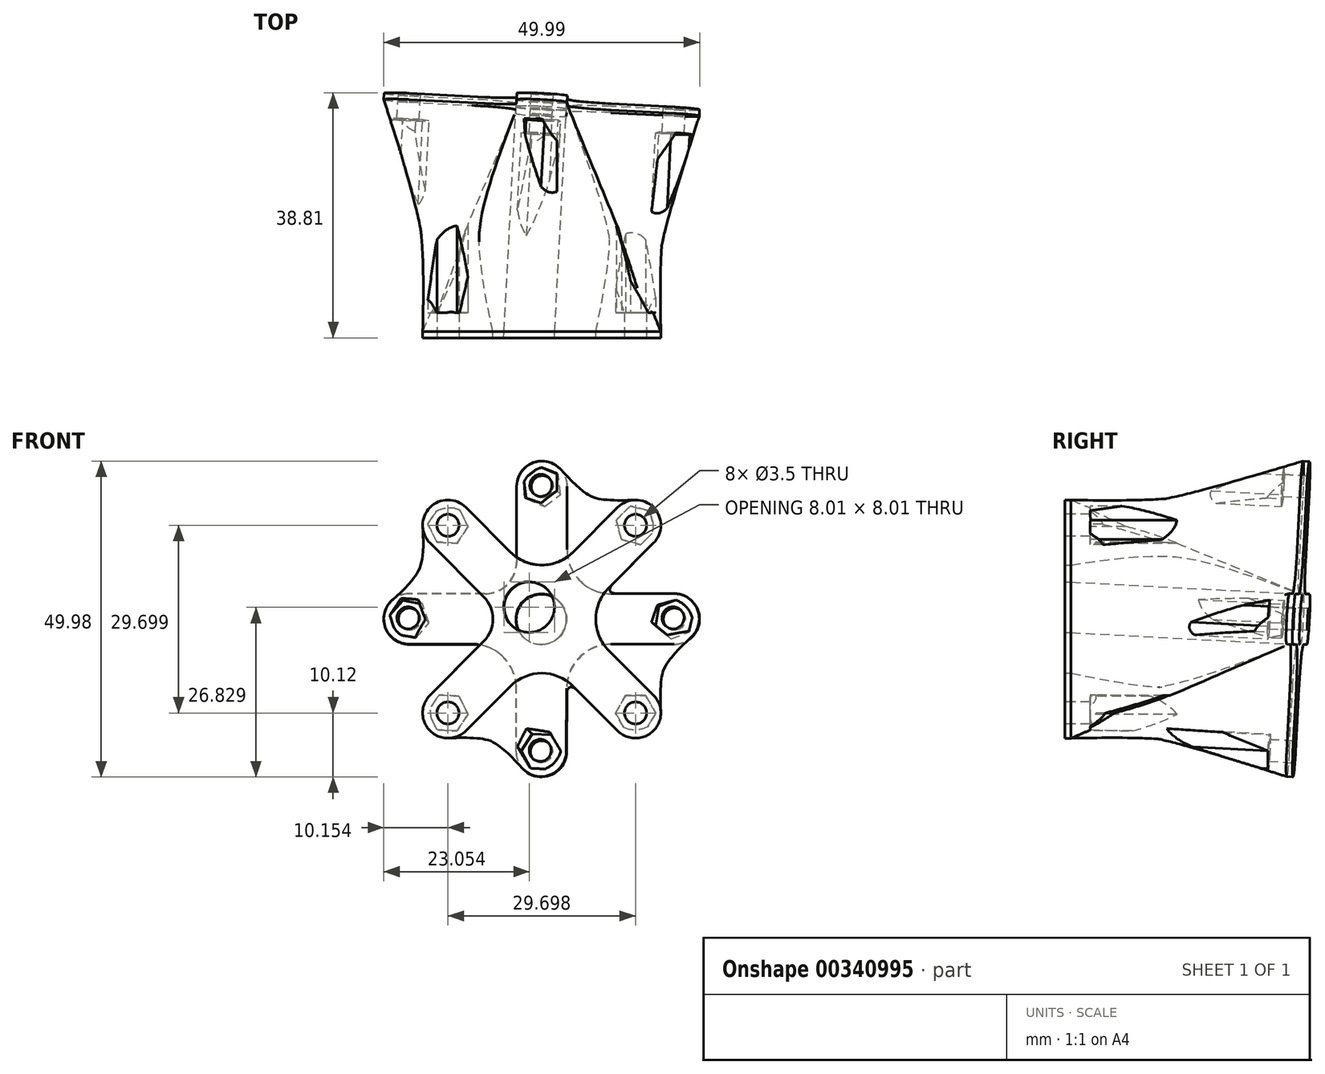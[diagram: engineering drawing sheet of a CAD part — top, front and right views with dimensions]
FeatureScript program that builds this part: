
annotation { "Feature Type Name" : "Feature", "Feature Type Description" : "" }
export const myFeature = defineFeature(function(context is Context, id is Id, definition is map)
    precondition{}
    {
        {
            var Q0;
            Q0=qCreatedBy(makeId("Front.planeOp"),FACE);
            var sketch = newSketch(context, id + "F0", { "sketchPlane" : qUnion([Q0])});
            skLineSegment(sketch, "E0", {"start": v(-2.67, 4.2) * mm, "end": v(-2.67, 70.2) * mm});
            skFitSpline(sketch, "E1", {"points": [v(-2.67, 70.2) * mm, v(4.36, 79.68) * mm, v(10.86, 84.56) * mm, v(19.6, 87.5) * mm, v(32.83, 88.7) * mm], "startDerivative": vector(17.44, 44.03) * mm, "endDerivative": vector(48.5, 0) * mm});
            skFitSpline(sketch, "E2", {"points": [v(-2.67, 4.2) * mm, v(0, -1.2) * mm, v(6.58, -5.59) * mm, v(16.1, -7.75) * mm, v(24.4, -8.77) * mm, v(32.83, -9.43) * mm], "startDerivative": vector(11.57, -32.78) * mm, "endDerivative": vector(34.9, 0) * mm});
            skFitSpline(sketch, "E3.MirrorCS", {"points": [v(68.33, 70.2) * mm, v(61.3, 79.68) * mm, v(54.8, 84.56) * mm, v(46.08, 87.5) * mm, v(32.83, 88.7) * mm], "startDerivative": vector(-17.44, 44.03) * mm, "endDerivative": vector(-48.5, 0) * mm});
            skLineSegment(sketch, "E4.MirrorCS", {"start": v(68.33, 4.2) * mm, "end": v(68.33, 70.2) * mm});
            skFitSpline(sketch, "E5.MirrorCS", {"points": [v(68.33, 4.2) * mm, v(65.67, -1.2) * mm, v(59.09, -5.59) * mm, v(49.56, -7.75) * mm, v(41.27, -8.77) * mm, v(32.83, -9.43) * mm], "startDerivative": vector(-11.57, -32.78) * mm, "endDerivative": vector(-34.9, 0) * mm});
            skCircle(sketch, "E6", {"center": v(16.13, 65.4) * mm, "radius": 1.75 * mm});
            skCircle(sketch, "E7", {"center": v(16.13, 36) * mm, "radius": 1.75 * mm});
            skCircle(sketch, "E8.MirrorC", {"center": v(45.53, 65.4) * mm, "radius": 1.75 * mm});
            skCircle(sketch, "E9.MirrorC", {"center": v(45.53, 36) * mm, "radius": 1.75 * mm});
            skCircle(sketch, "E10", {"center": v(30.83, 50.7) * mm, "radius": 10 * mm});
            skSolve(sketch);
        }
        {
            var Q0;
            Q0=qCreatedBy(makeId("Front.planeOp"),FACE);
            cPlane(context, id + "F1", {"entities" : qUnion([Q0]), "cplaneType" : CPlaneType.OFFSET, "offset" : 38 * mm, "oppositeDirection" : true, "width" : 150 * mm, "height" : 150 * mm});
        }
        {
            var Q0;
            Q0=qCreatedBy(id+"F1.planeOp",FACE);
            var sketch = newSketch(context, id + "F2", { "sketchPlane" : qUnion([Q0])});
            skLineSegment(sketch, "E11", {"start": v(30.83, 3.24) * mm, "end": v(30.83, 83.87) * mm, "construction": true});
            skLineSegment(sketch, "E12", {"start": v(-5.05, 50.7) * mm, "end": v(67.53, 50.7) * mm, "construction": true});
            skLineSegment(sketch, "E13", {"start": v(26.83, 71.7) * mm, "end": v(26.83, 59.7) * mm});
            skLineSegment(sketch, "E14.MirrorCS", {"start": v(34.83, 71.7) * mm, "end": v(34.83, 61.7) * mm});
            skArc(sketch, "E15", {"start": v(34.83, 71.7) * mm, "mid": v(30.83, 75.7) * mm, "end": v(26.83, 71.7) * mm});
            skArc(sketch, "E16.MirrorCS", {"start": v(34.83, 29.7) * mm, "mid": v(30.83, 25.7) * mm, "end": v(26.83, 29.7) * mm});
            skLineSegment(sketch, "E17", {"start": v(21.83, 54.7) * mm, "end": v(9.83, 54.7) * mm});
            skLineSegment(sketch, "E18.MirrorCS", {"start": v(51.83, 46.7) * mm, "end": v(41.83, 46.7) * mm});
            skArc(sketch, "E19", {"start": v(51.83, 54.7) * mm, "mid": v(55.83, 50.7) * mm, "end": v(51.83, 46.7) * mm});
            skArc(sketch, "E20.MirrorCS", {"start": v(9.83, 54.7) * mm, "mid": v(5.83, 50.7) * mm, "end": v(9.83, 46.7) * mm});
            skLineSegment(sketch, "E21", {"start": v(40.15, 65.4) * mm, "end": v(21.95, 65.4) * mm, "construction": true});
            skCircle(sketch, "E22", {"center": v(30.83, 71.7) * mm, "radius": 1.75 * mm});
            skCircle(sketch, "E23", {"center": v(30.83, 29.7) * mm, "radius": 1.75 * mm});
            skCircle(sketch, "E24", {"center": v(51.83, 50.7) * mm, "radius": 1.75 * mm});
            skCircle(sketch, "E25", {"center": v(9.83, 50.7) * mm, "radius": 1.75 * mm});
            skPoint(sketch, "E26.newPointA", {"position": v(26.83, 29.7) * mm});
            skPoint(sketch, "E26.newPointB", {"position": v(51.83, 54.7) * mm});
            skArc(sketch, "E26.filletArc", {"start": v(21.83, 54.7) * mm, "mid": v(25.37, 56.17) * mm, "end": v(26.83, 59.7) * mm});
            skLineSegment(sketch, "E27", {"start": v(51.83, 54.7) * mm, "end": v(41.83, 54.7) * mm});
            skLineSegment(sketch, "E28", {"start": v(26.83, 29.7) * mm, "end": v(26.83, 39.7) * mm});
            skPoint(sketch, "E29.newPointA", {"position": v(34.83, 29.7) * mm});
            skArc(sketch, "E29.filletArc", {"start": v(34.83, 61.7) * mm, "mid": v(36.88, 56.76) * mm, "end": v(41.83, 54.7) * mm});
            skLineSegment(sketch, "E30", {"start": v(34.83, 29.7) * mm, "end": v(34.83, 39.7) * mm});
            skPoint(sketch, "E31.newPointB", {"position": v(9.83, 46.7) * mm});
            skArc(sketch, "E31.filletArc", {"start": v(41.83, 46.7) * mm, "mid": v(36.88, 44.66) * mm, "end": v(34.83, 39.7) * mm});
            skLineSegment(sketch, "E32", {"start": v(9.83, 46.7) * mm, "end": v(19.83, 46.7) * mm});
            skArc(sketch, "E33.filletArc", {"start": v(26.83, 39.7) * mm, "mid": v(24.78, 44.66) * mm, "end": v(19.83, 46.7) * mm});
            skCircle(sketch, "E34", {"center": v(30.83, 50.7) * mm, "radius": 4 * mm});
            skSolve(sketch);
        }
        {
            var Q0;
            Q0=makeQuery(id+"F2.imprint","IMPRINT",FACE,{"disambiguationData":[TD([[makeQuery(id+"F2.imprint","IMPRINT",EDGE,{"derivedFrom":sQuery(id+"F2.wireOp",EDGE,"E23")}),1.0]])]});
            var Q1;
            Q1=makeQuery(id+"F2.imprint","IMPRINT",FACE,{"disambiguationData":[TD([[makeQuery(id+"F2.imprint","IMPRINT",EDGE,{"derivedFrom":sQuery(id+"F2.wireOp",EDGE,"E34")}),1.0]])]});
            var Q2;
            Q2=makeQuery(id+"F2.imprint","IMPRINT",FACE,{"disambiguationData":[TD([[makeQuery(id+"F2.imprint","IMPRINT",EDGE,{"derivedFrom":sQuery(id+"F2.wireOp",EDGE,"E25")}),1.0]])]});
            var Q3;
            Q3=makeQuery(id+"F2.imprint","IMPRINT",FACE,{"disambiguationData":[TD([[makeQuery(id+"F2.imprint","IMPRINT",EDGE,{"derivedFrom":sQuery(id+"F2.wireOp",EDGE,"E22")}),1.0]])]});
            var Q4;
            Q4=makeQuery(id+"F2.imprint","IMPRINT",FACE,{"disambiguationData":[TD([[makeQuery(id+"F2.imprint","IMPRINT",EDGE,{"derivedFrom":sQuery(id+"F2.wireOp",EDGE,"E24")}),1.0]])]});
            var Q5;
            Q5=makeQuery(id+"F2.imprint","IMPRINT",FACE,{"disambiguationData":[TD([[makeQuery(id+"F2.imprint","IMPRINT",EDGE,{"derivedFrom":sQuery(id+"F2.wireOp",EDGE,"E13")}),1.0]])]});
            extrude(context, id + "F3", {"entities" : qUnion([Q0, Q1, Q2, Q3, Q4, Q5]), "depth" : 1 * mm, "offsetDistance" : 25 * mm});
        }
        {
            var Q0;
            Q0=makeQuery(id+"F3.opExtrude","SWEPT_BODY",BODY,{"disambiguationData":[OSD([sQuery(id+"F2.wireOp",EDGE,"E13"),sQuery(id+"F2.wireOp",EDGE,"E14.MirrorCS"),sQuery(id+"F2.wireOp",EDGE,"E15"),sQuery(id+"F2.wireOp",EDGE,"E16.MirrorCS"),sQuery(id+"F2.wireOp",EDGE,"E17"),sQuery(id+"F2.wireOp",EDGE,"E18.MirrorCS"),sQuery(id+"F2.wireOp",EDGE,"E19"),sQuery(id+"F2.wireOp",EDGE,"E20.MirrorCS"),sQuery(id+"F2.wireOp",EDGE,"E26.filletArc"),sQuery(id+"F2.wireOp",EDGE,"E27"),sQuery(id+"F2.wireOp",EDGE,"E28"),sQuery(id+"F2.wireOp",EDGE,"E29.filletArc"),sQuery(id+"F2.wireOp",EDGE,"E30"),sQuery(id+"F2.wireOp",EDGE,"E31.filletArc"),sQuery(id+"F2.wireOp",EDGE,"E32"),sQuery(id+"F2.wireOp",EDGE,"E33.filletArc")])]});
            transform(context, id + "F4", {"entities" : qUnion([Q0]), "transformType" : TransformType.TRANSLATION_3D, "dx" : 0 * mm, "dy" : -36 * mm, "dz" : 0 * mm, "makeCopy" : true});
        }
        {
            var Q0;
            Q0=makeQuery(id+"F3.opExtrude","SWEPT_BODY",BODY,{"disambiguationData":[OSD([sQuery(id+"F2.wireOp",EDGE,"E13"),sQuery(id+"F2.wireOp",EDGE,"E14.MirrorCS"),sQuery(id+"F2.wireOp",EDGE,"E15"),sQuery(id+"F2.wireOp",EDGE,"E16.MirrorCS"),sQuery(id+"F2.wireOp",EDGE,"E17"),sQuery(id+"F2.wireOp",EDGE,"E18.MirrorCS"),sQuery(id+"F2.wireOp",EDGE,"E19"),sQuery(id+"F2.wireOp",EDGE,"E20.MirrorCS"),sQuery(id+"F2.wireOp",EDGE,"E26.filletArc"),sQuery(id+"F2.wireOp",EDGE,"E27"),sQuery(id+"F2.wireOp",EDGE,"E28"),sQuery(id+"F2.wireOp",EDGE,"E29.filletArc"),sQuery(id+"F2.wireOp",EDGE,"E30"),sQuery(id+"F2.wireOp",EDGE,"E31.filletArc"),sQuery(id+"F2.wireOp",EDGE,"E32"),sQuery(id+"F2.wireOp",EDGE,"E33.filletArc")])]});
            var Q1;
            Q1=makeQuery(id+"F3.opExtrude","CAP_EDGE",EDGE,{"disambiguationData":[OSD([sQuery(id+"F2.wireOp",EDGE,"E30")])],"isStart":true});
            transform(context, id + "F5", {"entities" : qUnion([Q0]), "transformType" : TransformType.ROTATION, "transformAxis" : qUnion([Q1]), "angle" : 3 * degree, "oppositeDirection" : true, "makeCopy" : false});
        }
        {
            var Q0;
            Q0=makeQuery(id+"F3.opExtrude","SWEPT_BODY",BODY,{"disambiguationData":[OSD([sQuery(id+"F2.wireOp",EDGE,"E13"),sQuery(id+"F2.wireOp",EDGE,"E14.MirrorCS"),sQuery(id+"F2.wireOp",EDGE,"E15"),sQuery(id+"F2.wireOp",EDGE,"E16.MirrorCS"),sQuery(id+"F2.wireOp",EDGE,"E17"),sQuery(id+"F2.wireOp",EDGE,"E18.MirrorCS"),sQuery(id+"F2.wireOp",EDGE,"E19"),sQuery(id+"F2.wireOp",EDGE,"E20.MirrorCS"),sQuery(id+"F2.wireOp",EDGE,"E26.filletArc"),sQuery(id+"F2.wireOp",EDGE,"E27"),sQuery(id+"F2.wireOp",EDGE,"E28"),sQuery(id+"F2.wireOp",EDGE,"E29.filletArc"),sQuery(id+"F2.wireOp",EDGE,"E30"),sQuery(id+"F2.wireOp",EDGE,"E31.filletArc"),sQuery(id+"F2.wireOp",EDGE,"E32"),sQuery(id+"F2.wireOp",EDGE,"E33.filletArc")])]});
            var Q1;
            Q1=makeQuery(id+"F3.opExtrude","CAP_EDGE",EDGE,{"disambiguationData":[OSD([sQuery(id+"F2.wireOp",EDGE,"E32")])],"isStart":true});
            transform(context, id + "F6", {"entities" : qUnion([Q0]), "transformType" : TransformType.ROTATION, "transformAxis" : qUnion([Q1]), "angle" : 3 * degree, "oppositeDirection" : true, "makeCopy" : false});
        }
        {
            var Q0;
            Q0=makeQuery(id+"F4.opPattern","COPY",BODY,{"derivedFrom":makeQuery(id+"FqoNIN35yEYZdyi_0.opExtrude","SWEPT_BODY",BODY,{"disambiguationData":[OSD([sQuery(id+"F2.wireOp",EDGE,"E13"),sQuery(id+"F2.wireOp",EDGE,"E14.MirrorCS"),sQuery(id+"F2.wireOp",EDGE,"E15"),sQuery(id+"F2.wireOp",EDGE,"E16.MirrorCS"),sQuery(id+"F2.wireOp",EDGE,"E17"),sQuery(id+"F2.wireOp",EDGE,"E18.MirrorCS"),sQuery(id+"F2.wireOp",EDGE,"E19"),sQuery(id+"F2.wireOp",EDGE,"E20.MirrorCS"),sQuery(id+"F2.wireOp",EDGE,"E22"),sQuery(id+"F2.wireOp",EDGE,"E23"),sQuery(id+"F2.wireOp",EDGE,"E24"),sQuery(id+"F2.wireOp",EDGE,"E25"),sQuery(id+"F2.wireOp",EDGE,"E26.filletArc"),sQuery(id+"F2.wireOp",EDGE,"E27"),sQuery(id+"F2.wireOp",EDGE,"E28"),sQuery(id+"F2.wireOp",EDGE,"E29.filletArc"),sQuery(id+"F2.wireOp",EDGE,"E30"),sQuery(id+"F2.wireOp",EDGE,"E31.filletArc"),sQuery(id+"F2.wireOp",EDGE,"E32"),sQuery(id+"F2.wireOp",EDGE,"E33.filletArc"),sQuery(id+"F2.wireOp",EDGE,"E34")])]}),"instanceName":"1"});
            var Q1;
            Q1=makeQuery(id+"F4.opPattern","COPY",BODY,{"derivedFrom":makeQuery(id+"F3.opExtrude","SWEPT_BODY",BODY,{"disambiguationData":[OSD([sQuery(id+"F2.wireOp",EDGE,"E13"),sQuery(id+"F2.wireOp",EDGE,"E14.MirrorCS"),sQuery(id+"F2.wireOp",EDGE,"E15"),sQuery(id+"F2.wireOp",EDGE,"E16.MirrorCS"),sQuery(id+"F2.wireOp",EDGE,"E17"),sQuery(id+"F2.wireOp",EDGE,"E18.MirrorCS"),sQuery(id+"F2.wireOp",EDGE,"E19"),sQuery(id+"F2.wireOp",EDGE,"E20.MirrorCS"),sQuery(id+"F2.wireOp",EDGE,"E26.filletArc"),sQuery(id+"F2.wireOp",EDGE,"E27"),sQuery(id+"F2.wireOp",EDGE,"E28"),sQuery(id+"F2.wireOp",EDGE,"E29.filletArc"),sQuery(id+"F2.wireOp",EDGE,"E30"),sQuery(id+"F2.wireOp",EDGE,"E31.filletArc"),sQuery(id+"F2.wireOp",EDGE,"E32"),sQuery(id+"F2.wireOp",EDGE,"E33.filletArc")])]}),"instanceName":"1"});
            var Q2;
            Q2=sQuery(id+"F0.wireOp",EDGE,"E10");
            transform(context, id + "F7", {"entities" : qUnion([Q0, Q1]), "transformType" : TransformType.ROTATION, "transformAxis" : qUnion([Q2]), "angle" : 45 * degree, "makeCopy" : false});
        }
        {
            var Q0;
            Q0=makeQuery(id+"F3.opExtrude","CAP_FACE",FACE,{"disambiguationData":[OSD([sQuery(id+"F2.wireOp",EDGE,"E13"),sQuery(id+"F2.wireOp",EDGE,"E14.MirrorCS"),sQuery(id+"F2.wireOp",EDGE,"E15"),sQuery(id+"F2.wireOp",EDGE,"E16.MirrorCS"),sQuery(id+"F2.wireOp",EDGE,"E17"),sQuery(id+"F2.wireOp",EDGE,"E18.MirrorCS"),sQuery(id+"F2.wireOp",EDGE,"E19"),sQuery(id+"F2.wireOp",EDGE,"E20.MirrorCS"),sQuery(id+"F2.wireOp",EDGE,"E26.filletArc"),sQuery(id+"F2.wireOp",EDGE,"E27"),sQuery(id+"F2.wireOp",EDGE,"E28"),sQuery(id+"F2.wireOp",EDGE,"E29.filletArc"),sQuery(id+"F2.wireOp",EDGE,"E30"),sQuery(id+"F2.wireOp",EDGE,"E31.filletArc"),sQuery(id+"F2.wireOp",EDGE,"E32"),sQuery(id+"F2.wireOp",EDGE,"E33.filletArc")])],"isStart":false});
            var Q1;
            Q1=makeQuery(id+"F4.opPattern","COPY",FACE,{"derivedFrom":makeQuery(id+"F3.opExtrude","CAP_FACE",FACE,{"disambiguationData":[OSD([sQuery(id+"F2.wireOp",EDGE,"E13"),sQuery(id+"F2.wireOp",EDGE,"E14.MirrorCS"),sQuery(id+"F2.wireOp",EDGE,"E15"),sQuery(id+"F2.wireOp",EDGE,"E16.MirrorCS"),sQuery(id+"F2.wireOp",EDGE,"E17"),sQuery(id+"F2.wireOp",EDGE,"E18.MirrorCS"),sQuery(id+"F2.wireOp",EDGE,"E19"),sQuery(id+"F2.wireOp",EDGE,"E20.MirrorCS"),sQuery(id+"F2.wireOp",EDGE,"E26.filletArc"),sQuery(id+"F2.wireOp",EDGE,"E27"),sQuery(id+"F2.wireOp",EDGE,"E28"),sQuery(id+"F2.wireOp",EDGE,"E29.filletArc"),sQuery(id+"F2.wireOp",EDGE,"E30"),sQuery(id+"F2.wireOp",EDGE,"E31.filletArc"),sQuery(id+"F2.wireOp",EDGE,"E32"),sQuery(id+"F2.wireOp",EDGE,"E33.filletArc")])],"isStart":true}),"instanceName":"1"});
            loft(context, id + "F8", {"sheetProfilesArray" : [{ "sheetProfileEntities" : qUnion([Q0]) }, { "sheetProfileEntities" : qUnion([Q1]) }]});
        }
        {
            var Q0;
            Q0=makeQuery(id+"F4.opPattern","COPY",FACE,{"derivedFrom":makeQuery(id+"F3.opExtrude","CAP_FACE",FACE,{"disambiguationData":[OSD([sQuery(id+"F2.wireOp",EDGE,"E13"),sQuery(id+"F2.wireOp",EDGE,"E14.MirrorCS"),sQuery(id+"F2.wireOp",EDGE,"E15"),sQuery(id+"F2.wireOp",EDGE,"E16.MirrorCS"),sQuery(id+"F2.wireOp",EDGE,"E17"),sQuery(id+"F2.wireOp",EDGE,"E18.MirrorCS"),sQuery(id+"F2.wireOp",EDGE,"E19"),sQuery(id+"F2.wireOp",EDGE,"E20.MirrorCS"),sQuery(id+"F2.wireOp",EDGE,"E26.filletArc"),sQuery(id+"F2.wireOp",EDGE,"E27"),sQuery(id+"F2.wireOp",EDGE,"E28"),sQuery(id+"F2.wireOp",EDGE,"E29.filletArc"),sQuery(id+"F2.wireOp",EDGE,"E30"),sQuery(id+"F2.wireOp",EDGE,"E31.filletArc"),sQuery(id+"F2.wireOp",EDGE,"E32"),sQuery(id+"F2.wireOp",EDGE,"E33.filletArc")])],"isStart":false}),"instanceName":"1"});
            var sketch = newSketch(context, id + "F9", { "sketchPlane" : qUnion([Q0])});
            skLineSegment(sketch, "E35", {"start": v(48.51, 68.39) * mm, "end": v(13.16, 33.03) * mm, "construction": true});
            skLineSegment(sketch, "E36", {"start": v(13.16, 68.39) * mm, "end": v(48.51, 33.03) * mm, "construction": true});
            skCircle(sketch, "E37", {"center": v(45.68, 35.86) * mm, "radius": 1.75 * mm});
            skCircle(sketch, "E38", {"center": v(45.68, 65.56) * mm, "radius": 1.75 * mm});
            skCircle(sketch, "E39", {"center": v(15.98, 35.86) * mm, "radius": 1.75 * mm});
            skCircle(sketch, "E40", {"center": v(15.98, 65.56) * mm, "radius": 1.75 * mm});
            skSolve(sketch);
        }
        {
            var Q0;
            Q0=makeQuery(id+"F9.imprint","IMPRINT",FACE,{"disambiguationData":[TD([[makeQuery(id+"F9.imprint","IMPRINT",EDGE,{"derivedFrom":sQuery(id+"F9.wireOp",EDGE,"E40")}),1.0]])]});
            var Q1;
            Q1=makeQuery(id+"F9.imprint","IMPRINT",FACE,{"disambiguationData":[TD([[makeQuery(id+"F9.imprint","IMPRINT",EDGE,{"derivedFrom":sQuery(id+"F9.wireOp",EDGE,"E38")}),1.0]])]});
            var Q2;
            Q2=makeQuery(id+"F9.imprint","IMPRINT",FACE,{"disambiguationData":[TD([[makeQuery(id+"F9.imprint","IMPRINT",EDGE,{"derivedFrom":sQuery(id+"F9.wireOp",EDGE,"E39")}),1.0]])]});
            var Q3;
            Q3=makeQuery(id+"F9.imprint","IMPRINT",FACE,{"disambiguationData":[TD([[makeQuery(id+"F9.imprint","IMPRINT",EDGE,{"derivedFrom":sQuery(id+"F9.wireOp",EDGE,"E37")}),1.0]])]});
            extrude(context, id + "F10", {"entities" : qUnion([Q0, Q1, Q2, Q3]), "oppositeDirection" : true, "depth" : 25 * mm, "offsetDistance" : 25 * mm});
        }
        {
            var Q0;
            Q0=makeQuery(id+"F10.opExtrude","SWEPT_BODY",BODY,{"disambiguationData":[OSD([sQuery(id+"F9.wireOp",EDGE,"E40")])]});
            var Q1;
            Q1=makeQuery(id+"F10.opExtrude","SWEPT_BODY",BODY,{"disambiguationData":[OSD([sQuery(id+"F9.wireOp",EDGE,"E39")])]});
            var Q2;
            Q2=makeQuery(id+"F10.opExtrude","SWEPT_BODY",BODY,{"disambiguationData":[OSD([sQuery(id+"F9.wireOp",EDGE,"E38")])]});
            var Q3;
            Q3=makeQuery(id+"F10.opExtrude","SWEPT_BODY",BODY,{"disambiguationData":[OSD([sQuery(id+"F9.wireOp",EDGE,"E37")])]});
            var Q4;
            Q4=makeQuery(id+"F8.opLoft","SWEPT_BODY",BODY,{"disambiguationData":[OSD([sQuery(id+"F2.wireOp",EDGE,"E13"),sQuery(id+"F2.wireOp",EDGE,"E14.MirrorCS"),sQuery(id+"F2.wireOp",EDGE,"E15"),sQuery(id+"F2.wireOp",EDGE,"E16.MirrorCS"),sQuery(id+"F2.wireOp",EDGE,"E17"),sQuery(id+"F2.wireOp",EDGE,"E18.MirrorCS"),sQuery(id+"F2.wireOp",EDGE,"E19"),sQuery(id+"F2.wireOp",EDGE,"E20.MirrorCS"),sQuery(id+"F2.wireOp",EDGE,"E26.filletArc"),sQuery(id+"F2.wireOp",EDGE,"E27"),sQuery(id+"F2.wireOp",EDGE,"E28"),sQuery(id+"F2.wireOp",EDGE,"E29.filletArc"),sQuery(id+"F2.wireOp",EDGE,"E30"),sQuery(id+"F2.wireOp",EDGE,"E31.filletArc"),sQuery(id+"F2.wireOp",EDGE,"E32"),sQuery(id+"F2.wireOp",EDGE,"E33.filletArc")])]});
            var Q5;
            Q5=makeQuery(id+"F4.opPattern","COPY",BODY,{"derivedFrom":makeQuery(id+"F3.opExtrude","SWEPT_BODY",BODY,{"disambiguationData":[OSD([sQuery(id+"F2.wireOp",EDGE,"E13"),sQuery(id+"F2.wireOp",EDGE,"E14.MirrorCS"),sQuery(id+"F2.wireOp",EDGE,"E15"),sQuery(id+"F2.wireOp",EDGE,"E16.MirrorCS"),sQuery(id+"F2.wireOp",EDGE,"E17"),sQuery(id+"F2.wireOp",EDGE,"E18.MirrorCS"),sQuery(id+"F2.wireOp",EDGE,"E19"),sQuery(id+"F2.wireOp",EDGE,"E20.MirrorCS"),sQuery(id+"F2.wireOp",EDGE,"E26.filletArc"),sQuery(id+"F2.wireOp",EDGE,"E27"),sQuery(id+"F2.wireOp",EDGE,"E28"),sQuery(id+"F2.wireOp",EDGE,"E29.filletArc"),sQuery(id+"F2.wireOp",EDGE,"E30"),sQuery(id+"F2.wireOp",EDGE,"E31.filletArc"),sQuery(id+"F2.wireOp",EDGE,"E32"),sQuery(id+"F2.wireOp",EDGE,"E33.filletArc")])]}),"instanceName":"1"});
            var Q6;
            Q6=makeQuery(id+"F3.opExtrude","SWEPT_BODY",BODY,{"disambiguationData":[OSD([sQuery(id+"F2.wireOp",EDGE,"E13"),sQuery(id+"F2.wireOp",EDGE,"E14.MirrorCS"),sQuery(id+"F2.wireOp",EDGE,"E15"),sQuery(id+"F2.wireOp",EDGE,"E16.MirrorCS"),sQuery(id+"F2.wireOp",EDGE,"E17"),sQuery(id+"F2.wireOp",EDGE,"E18.MirrorCS"),sQuery(id+"F2.wireOp",EDGE,"E19"),sQuery(id+"F2.wireOp",EDGE,"E20.MirrorCS"),sQuery(id+"F2.wireOp",EDGE,"E26.filletArc"),sQuery(id+"F2.wireOp",EDGE,"E27"),sQuery(id+"F2.wireOp",EDGE,"E28"),sQuery(id+"F2.wireOp",EDGE,"E29.filletArc"),sQuery(id+"F2.wireOp",EDGE,"E30"),sQuery(id+"F2.wireOp",EDGE,"E31.filletArc"),sQuery(id+"F2.wireOp",EDGE,"E32"),sQuery(id+"F2.wireOp",EDGE,"E33.filletArc")])]});
            booleanBodies(context, id + "F11", {"operationType" : BooleanOperationType.SUBTRACTION, "tools" : qUnion([Q0, Q1, Q2, Q3]), "targets" : qUnion([Q4, Q5, Q6])});
        }
        {
            var Q0;
            Q0=makeQuery(id+"F3.opExtrude","CAP_FACE",FACE,{"disambiguationData":[OSD([sQuery(id+"F2.wireOp",EDGE,"E13"),sQuery(id+"F2.wireOp",EDGE,"E14.MirrorCS"),sQuery(id+"F2.wireOp",EDGE,"E15"),sQuery(id+"F2.wireOp",EDGE,"E16.MirrorCS"),sQuery(id+"F2.wireOp",EDGE,"E17"),sQuery(id+"F2.wireOp",EDGE,"E18.MirrorCS"),sQuery(id+"F2.wireOp",EDGE,"E19"),sQuery(id+"F2.wireOp",EDGE,"E20.MirrorCS"),sQuery(id+"F2.wireOp",EDGE,"E26.filletArc"),sQuery(id+"F2.wireOp",EDGE,"E27"),sQuery(id+"F2.wireOp",EDGE,"E28"),sQuery(id+"F2.wireOp",EDGE,"E29.filletArc"),sQuery(id+"F2.wireOp",EDGE,"E30"),sQuery(id+"F2.wireOp",EDGE,"E31.filletArc"),sQuery(id+"F2.wireOp",EDGE,"E32"),sQuery(id+"F2.wireOp",EDGE,"E33.filletArc")])],"isStart":true});
            var sketch = newSketch(context, id + "F12", { "sketchPlane" : qUnion([Q0])});
            skCircle(sketch, "E41.cCircle", {"center": v(-29, 73.65) * mm, "radius": 2.75 * mm, "construction": true});
            skLineSegment(sketch, "E41.0", {"start": v(-26.45, 71.75) * mm, "end": v(-29.37, 70.5) * mm});
            skLineSegment(sketch, "E41.1", {"start": v(-29.37, 70.5) * mm, "end": v(-31.92, 72.4) * mm});
            skLineSegment(sketch, "E41.2", {"start": v(-31.92, 72.4) * mm, "end": v(-31.55, 75.54) * mm});
            skLineSegment(sketch, "E41.3", {"start": v(-31.55, 75.54) * mm, "end": v(-28.63, 76.8) * mm});
            skLineSegment(sketch, "E41.4", {"start": v(-28.63, 76.8) * mm, "end": v(-26.08, 74.9) * mm});
            skLineSegment(sketch, "E41.5", {"start": v(-26.08, 74.9) * mm, "end": v(-26.45, 71.75) * mm});
            skPoint(sketch, "E41.0.midPoint", {"position": v(-27.91, 71.12) * mm});
            skCircle(sketch, "E42.cCircle", {"center": v(-7.94, 52.7) * mm, "radius": 2.75 * mm, "construction": true});
            skLineSegment(sketch, "E42.0", {"start": v(-5.84, 50.32) * mm, "end": v(-8.96, 49.7) * mm});
            skLineSegment(sketch, "E42.1", {"start": v(-8.96, 49.7) * mm, "end": v(-11.05, 52.08) * mm});
            skLineSegment(sketch, "E42.2", {"start": v(-11.05, 52.08) * mm, "end": v(-10.04, 55.09) * mm});
            skLineSegment(sketch, "E42.3", {"start": v(-10.04, 55.09) * mm, "end": v(-6.93, 55.71) * mm});
            skLineSegment(sketch, "E42.4", {"start": v(-6.93, 55.71) * mm, "end": v(-4.83, 53.33) * mm});
            skLineSegment(sketch, "E42.5", {"start": v(-4.83, 53.33) * mm, "end": v(-5.84, 50.32) * mm});
            skPoint(sketch, "E42.0.midPoint", {"position": v(-7.4, 50) * mm});
            skCircle(sketch, "E43.cCircle", {"center": v(-28.88, 31.65) * mm, "radius": 2.75 * mm, "construction": true});
            skLineSegment(sketch, "E43.0", {"start": v(-25.71, 31.76) * mm, "end": v(-27.2, 28.96) * mm});
            skLineSegment(sketch, "E43.1", {"start": v(-27.2, 28.96) * mm, "end": v(-30.37, 28.84) * mm});
            skLineSegment(sketch, "E43.2", {"start": v(-30.37, 28.84) * mm, "end": v(-32.06, 31.54) * mm});
            skLineSegment(sketch, "E43.3", {"start": v(-32.06, 31.54) * mm, "end": v(-30.57, 34.34) * mm});
            skLineSegment(sketch, "E43.4", {"start": v(-30.57, 34.34) * mm, "end": v(-27.4, 34.45) * mm});
            skLineSegment(sketch, "E43.5", {"start": v(-27.4, 34.45) * mm, "end": v(-25.71, 31.76) * mm});
            skPoint(sketch, "E43.0.midPoint", {"position": v(-26.45, 30.36) * mm});
            skCircle(sketch, "E44.cCircle", {"center": v(-49.94, 52.6) * mm, "radius": 2.75 * mm, "construction": true});
            skLineSegment(sketch, "E44.0", {"start": v(-46.97, 51.48) * mm, "end": v(-49.41, 49.46) * mm});
            skLineSegment(sketch, "E44.1", {"start": v(-49.41, 49.46) * mm, "end": v(-52.4, 50.57) * mm});
            skLineSegment(sketch, "E44.2", {"start": v(-52.4, 50.57) * mm, "end": v(-52.92, 53.7) * mm});
            skLineSegment(sketch, "E44.3", {"start": v(-52.92, 53.7) * mm, "end": v(-50.47, 55.72) * mm});
            skLineSegment(sketch, "E44.4", {"start": v(-50.47, 55.72) * mm, "end": v(-47.5, 54.61) * mm});
            skLineSegment(sketch, "E44.5", {"start": v(-47.5, 54.61) * mm, "end": v(-46.97, 51.48) * mm});
            skPoint(sketch, "E44.0.midPoint", {"position": v(-48.2, 50.47) * mm});
            skSolve(sketch);
        }
        {
            var Q0;
            Q0=makeQuery(id+"F12.imprint","IMPRINT",FACE,{"disambiguationData":[TD([[makeQuery(id+"F12.imprint","IMPRINT",EDGE,{"derivedFrom":sQuery(id+"F12.wireOp",EDGE,"E44.0")}),-1.0]])]});
            var Q1;
            Q1=makeQuery(id+"F12.imprint","IMPRINT",FACE,{"disambiguationData":[TD([[makeQuery(id+"F12.imprint","IMPRINT",EDGE,{"derivedFrom":sQuery(id+"F12.wireOp",EDGE,"E42.0")}),-1.0]])]});
            var Q2;
            Q2=makeQuery(id+"F12.imprint","IMPRINT",FACE,{"disambiguationData":[TD([[makeQuery(id+"F12.imprint","IMPRINT",EDGE,{"derivedFrom":sQuery(id+"F12.wireOp",EDGE,"E43.0")}),-1.0]])]});
            var Q3;
            Q3=makeQuery(id+"F12.imprint","IMPRINT",FACE,{"disambiguationData":[TD([[makeQuery(id+"F12.imprint","IMPRINT",EDGE,{"derivedFrom":sQuery(id+"F12.wireOp",EDGE,"E41.0")}),-1.0]])]});
            extrude(context, id + "F13", {"entities" : qUnion([Q0, Q1, Q2, Q3]), "oppositeDirection" : true, "depth" : 25 * mm, "offsetDistance" : 25 * mm});
        }
        {
            var Q0;
            Q0=makeQuery(id+"F13.opExtrude","SWEPT_BODY",BODY,{"disambiguationData":[OSD([sQuery(id+"F12.wireOp",EDGE,"E44.0"),sQuery(id+"F12.wireOp",EDGE,"E44.1"),sQuery(id+"F12.wireOp",EDGE,"E44.2"),sQuery(id+"F12.wireOp",EDGE,"E44.3"),sQuery(id+"F12.wireOp",EDGE,"E44.4"),sQuery(id+"F12.wireOp",EDGE,"E44.5")])]});
            var Q1;
            Q1=makeQuery(id+"F13.opExtrude","SWEPT_BODY",BODY,{"disambiguationData":[OSD([sQuery(id+"F12.wireOp",EDGE,"E43.0"),sQuery(id+"F12.wireOp",EDGE,"E43.1"),sQuery(id+"F12.wireOp",EDGE,"E43.2"),sQuery(id+"F12.wireOp",EDGE,"E43.3"),sQuery(id+"F12.wireOp",EDGE,"E43.4"),sQuery(id+"F12.wireOp",EDGE,"E43.5")])]});
            var Q2;
            Q2=makeQuery(id+"F13.opExtrude","SWEPT_BODY",BODY,{"disambiguationData":[OSD([sQuery(id+"F12.wireOp",EDGE,"E42.0"),sQuery(id+"F12.wireOp",EDGE,"E42.1"),sQuery(id+"F12.wireOp",EDGE,"E42.2"),sQuery(id+"F12.wireOp",EDGE,"E42.3"),sQuery(id+"F12.wireOp",EDGE,"E42.4"),sQuery(id+"F12.wireOp",EDGE,"E42.5")])]});
            var Q3;
            Q3=makeQuery(id+"F13.opExtrude","SWEPT_BODY",BODY,{"disambiguationData":[OSD([sQuery(id+"F12.wireOp",EDGE,"E41.0"),sQuery(id+"F12.wireOp",EDGE,"E41.1"),sQuery(id+"F12.wireOp",EDGE,"E41.2"),sQuery(id+"F12.wireOp",EDGE,"E41.3"),sQuery(id+"F12.wireOp",EDGE,"E41.4"),sQuery(id+"F12.wireOp",EDGE,"E41.5")])]});
            transform(context, id + "F14", {"entities" : qUnion([Q0, Q1, Q2, Q3]), "transformType" : TransformType.TRANSLATION_3D, "dx" : 0 * mm, "dy" : -4 * mm, "dz" : 0 * mm, "makeCopy" : false});
        }
        {
            var Q0;
            Q0=makeQuery(id+"F13.opExtrude","SWEPT_BODY",BODY,{"disambiguationData":[OSD([sQuery(id+"F12.wireOp",EDGE,"E44.0"),sQuery(id+"F12.wireOp",EDGE,"E44.1"),sQuery(id+"F12.wireOp",EDGE,"E44.2"),sQuery(id+"F12.wireOp",EDGE,"E44.3"),sQuery(id+"F12.wireOp",EDGE,"E44.4"),sQuery(id+"F12.wireOp",EDGE,"E44.5")])]});
            var Q1;
            Q1=makeQuery(id+"F13.opExtrude","SWEPT_BODY",BODY,{"disambiguationData":[OSD([sQuery(id+"F12.wireOp",EDGE,"E43.0"),sQuery(id+"F12.wireOp",EDGE,"E43.1"),sQuery(id+"F12.wireOp",EDGE,"E43.2"),sQuery(id+"F12.wireOp",EDGE,"E43.3"),sQuery(id+"F12.wireOp",EDGE,"E43.4"),sQuery(id+"F12.wireOp",EDGE,"E43.5")])]});
            var Q2;
            Q2=makeQuery(id+"F13.opExtrude","SWEPT_BODY",BODY,{"disambiguationData":[OSD([sQuery(id+"F12.wireOp",EDGE,"E42.0"),sQuery(id+"F12.wireOp",EDGE,"E42.1"),sQuery(id+"F12.wireOp",EDGE,"E42.2"),sQuery(id+"F12.wireOp",EDGE,"E42.3"),sQuery(id+"F12.wireOp",EDGE,"E42.4"),sQuery(id+"F12.wireOp",EDGE,"E42.5")])]});
            var Q3;
            Q3=makeQuery(id+"F13.opExtrude","SWEPT_BODY",BODY,{"disambiguationData":[OSD([sQuery(id+"F12.wireOp",EDGE,"E41.0"),sQuery(id+"F12.wireOp",EDGE,"E41.1"),sQuery(id+"F12.wireOp",EDGE,"E41.2"),sQuery(id+"F12.wireOp",EDGE,"E41.3"),sQuery(id+"F12.wireOp",EDGE,"E41.4"),sQuery(id+"F12.wireOp",EDGE,"E41.5")])]});
            var Q4;
            Q4=makeQuery(id+"F8.opLoft","SWEPT_BODY",BODY,{"disambiguationData":[OSD([sQuery(id+"F2.wireOp",EDGE,"E13"),sQuery(id+"F2.wireOp",EDGE,"E14.MirrorCS"),sQuery(id+"F2.wireOp",EDGE,"E15"),sQuery(id+"F2.wireOp",EDGE,"E16.MirrorCS"),sQuery(id+"F2.wireOp",EDGE,"E17"),sQuery(id+"F2.wireOp",EDGE,"E18.MirrorCS"),sQuery(id+"F2.wireOp",EDGE,"E19"),sQuery(id+"F2.wireOp",EDGE,"E20.MirrorCS"),sQuery(id+"F2.wireOp",EDGE,"E26.filletArc"),sQuery(id+"F2.wireOp",EDGE,"E27"),sQuery(id+"F2.wireOp",EDGE,"E28"),sQuery(id+"F2.wireOp",EDGE,"E29.filletArc"),sQuery(id+"F2.wireOp",EDGE,"E30"),sQuery(id+"F2.wireOp",EDGE,"E31.filletArc"),sQuery(id+"F2.wireOp",EDGE,"E32"),sQuery(id+"F2.wireOp",EDGE,"E33.filletArc")])]});
            booleanBodies(context, id + "F15", {"operationType" : BooleanOperationType.SUBTRACTION, "tools" : qUnion([Q0, Q1, Q2, Q3]), "targets" : qUnion([Q4])});
        }
        {
            var Q0;
            Q0=makeQuery(id+"F3.opExtrude","CAP_FACE",FACE,{"disambiguationData":[OSD([sQuery(id+"F2.wireOp",EDGE,"E13"),sQuery(id+"F2.wireOp",EDGE,"E14.MirrorCS"),sQuery(id+"F2.wireOp",EDGE,"E15"),sQuery(id+"F2.wireOp",EDGE,"E16.MirrorCS"),sQuery(id+"F2.wireOp",EDGE,"E17"),sQuery(id+"F2.wireOp",EDGE,"E18.MirrorCS"),sQuery(id+"F2.wireOp",EDGE,"E19"),sQuery(id+"F2.wireOp",EDGE,"E20.MirrorCS"),sQuery(id+"F2.wireOp",EDGE,"E26.filletArc"),sQuery(id+"F2.wireOp",EDGE,"E27"),sQuery(id+"F2.wireOp",EDGE,"E28"),sQuery(id+"F2.wireOp",EDGE,"E29.filletArc"),sQuery(id+"F2.wireOp",EDGE,"E30"),sQuery(id+"F2.wireOp",EDGE,"E31.filletArc"),sQuery(id+"F2.wireOp",EDGE,"E32"),sQuery(id+"F2.wireOp",EDGE,"E33.filletArc")])],"isStart":true});
            var sketch = newSketch(context, id + "F16", { "sketchPlane" : qUnion([Q0])});
            skCircle(sketch, "E45", {"center": v(-29, 73.65) * mm, "radius": 1.75 * mm});
            skCircle(sketch, "E46", {"center": v(-7.94, 52.7) * mm, "radius": 1.75 * mm});
            skCircle(sketch, "E47", {"center": v(-49.94, 52.6) * mm, "radius": 1.75 * mm});
            skCircle(sketch, "E48", {"center": v(-28.88, 31.65) * mm, "radius": 1.75 * mm});
            skLineSegment(sketch, "E49", {"start": v(-53.94, 52.6) * mm, "end": v(0, 52.6) * mm, "construction": true});
            skPoint(sketch, "E49.startSnap0", {"position": v(-53.94, 52.58) * mm});
            skLineSegment(sketch, "E50", {"start": v(-28.88, 31.65) * mm, "end": v(-28.88, 80.58) * mm, "construction": true});
            skCircle(sketch, "E51", {"center": v(-28.88, 52.6) * mm, "radius": 4 * mm});
            skPoint(sketch, "E51.centerSnap0", {"position": v(-28.88, 56.11) * mm});
            skSolve(sketch);
        }
        {
            var Q0;
            Q0=makeQuery(id+"F16.imprint","IMPRINT",FACE,{"disambiguationData":[TD([[makeQuery(id+"F16.imprint","IMPRINT",EDGE,{"derivedFrom":sQuery(id+"F16.wireOp",EDGE,"E45")}),1.0]])]});
            var Q1;
            Q1=makeQuery(id+"F16.imprint","IMPRINT",FACE,{"disambiguationData":[TD([[makeQuery(id+"F16.imprint","IMPRINT",EDGE,{"derivedFrom":sQuery(id+"F16.wireOp",EDGE,"E47")}),1.0]])]});
            var Q2;
            Q2=makeQuery(id+"F16.imprint","IMPRINT",FACE,{"disambiguationData":[TD([[makeQuery(id+"F16.imprint","IMPRINT",EDGE,{"derivedFrom":sQuery(id+"F16.wireOp",EDGE,"E46")}),1.0]])]});
            var Q3;
            Q3=makeQuery(id+"F16.imprint","IMPRINT",FACE,{"disambiguationData":[TD([[makeQuery(id+"F16.imprint","IMPRINT",EDGE,{"derivedFrom":sQuery(id+"F16.wireOp",EDGE,"E48")}),1.0]])]});
            extrude(context, id + "F17", {"entities" : qUnion([Q0, Q1, Q2, Q3]), "oppositeDirection" : true, "depth" : 25 * mm, "offsetDistance" : 25 * mm});
        }
        {
            var Q0;
            Q0=makeQuery(id+"F17.opExtrude","SWEPT_BODY",BODY,{"disambiguationData":[OSD([sQuery(id+"F16.wireOp",EDGE,"E48")])]});
            var Q1;
            Q1=makeQuery(id+"F17.opExtrude","SWEPT_BODY",BODY,{"disambiguationData":[OSD([sQuery(id+"F16.wireOp",EDGE,"E47")])]});
            var Q2;
            Q2=makeQuery(id+"F17.opExtrude","SWEPT_BODY",BODY,{"disambiguationData":[OSD([sQuery(id+"F16.wireOp",EDGE,"E46")])]});
            var Q3;
            Q3=makeQuery(id+"F17.opExtrude","SWEPT_BODY",BODY,{"disambiguationData":[OSD([sQuery(id+"F16.wireOp",EDGE,"E45")])]});
            var Q4;
            Q4=makeQuery(id+"F3.opExtrude","SWEPT_BODY",BODY,{"disambiguationData":[OSD([sQuery(id+"F2.wireOp",EDGE,"E13"),sQuery(id+"F2.wireOp",EDGE,"E14.MirrorCS"),sQuery(id+"F2.wireOp",EDGE,"E15"),sQuery(id+"F2.wireOp",EDGE,"E16.MirrorCS"),sQuery(id+"F2.wireOp",EDGE,"E17"),sQuery(id+"F2.wireOp",EDGE,"E18.MirrorCS"),sQuery(id+"F2.wireOp",EDGE,"E19"),sQuery(id+"F2.wireOp",EDGE,"E20.MirrorCS"),sQuery(id+"F2.wireOp",EDGE,"E26.filletArc"),sQuery(id+"F2.wireOp",EDGE,"E27"),sQuery(id+"F2.wireOp",EDGE,"E28"),sQuery(id+"F2.wireOp",EDGE,"E29.filletArc"),sQuery(id+"F2.wireOp",EDGE,"E30"),sQuery(id+"F2.wireOp",EDGE,"E31.filletArc"),sQuery(id+"F2.wireOp",EDGE,"E32"),sQuery(id+"F2.wireOp",EDGE,"E33.filletArc")])]});
            var Q5;
            Q5=makeQuery(id+"F8.opLoft","SWEPT_BODY",BODY,{"disambiguationData":[OSD([sQuery(id+"F2.wireOp",EDGE,"E13"),sQuery(id+"F2.wireOp",EDGE,"E14.MirrorCS"),sQuery(id+"F2.wireOp",EDGE,"E15"),sQuery(id+"F2.wireOp",EDGE,"E16.MirrorCS"),sQuery(id+"F2.wireOp",EDGE,"E17"),sQuery(id+"F2.wireOp",EDGE,"E18.MirrorCS"),sQuery(id+"F2.wireOp",EDGE,"E19"),sQuery(id+"F2.wireOp",EDGE,"E20.MirrorCS"),sQuery(id+"F2.wireOp",EDGE,"E26.filletArc"),sQuery(id+"F2.wireOp",EDGE,"E27"),sQuery(id+"F2.wireOp",EDGE,"E28"),sQuery(id+"F2.wireOp",EDGE,"E29.filletArc"),sQuery(id+"F2.wireOp",EDGE,"E30"),sQuery(id+"F2.wireOp",EDGE,"E31.filletArc"),sQuery(id+"F2.wireOp",EDGE,"E32"),sQuery(id+"F2.wireOp",EDGE,"E33.filletArc")])]});
            booleanBodies(context, id + "F18", {"operationType" : BooleanOperationType.SUBTRACTION, "tools" : qUnion([Q0, Q1, Q2, Q3]), "targets" : qUnion([Q4, Q5])});
        }
        {
            var Q0;
            Q0=makeQuery(id+"F4.opPattern","COPY",FACE,{"derivedFrom":makeQuery(id+"F3.opExtrude","CAP_FACE",FACE,{"disambiguationData":[OSD([sQuery(id+"F2.wireOp",EDGE,"E13"),sQuery(id+"F2.wireOp",EDGE,"E14.MirrorCS"),sQuery(id+"F2.wireOp",EDGE,"E15"),sQuery(id+"F2.wireOp",EDGE,"E16.MirrorCS"),sQuery(id+"F2.wireOp",EDGE,"E17"),sQuery(id+"F2.wireOp",EDGE,"E18.MirrorCS"),sQuery(id+"F2.wireOp",EDGE,"E19"),sQuery(id+"F2.wireOp",EDGE,"E20.MirrorCS"),sQuery(id+"F2.wireOp",EDGE,"E26.filletArc"),sQuery(id+"F2.wireOp",EDGE,"E27"),sQuery(id+"F2.wireOp",EDGE,"E28"),sQuery(id+"F2.wireOp",EDGE,"E29.filletArc"),sQuery(id+"F2.wireOp",EDGE,"E30"),sQuery(id+"F2.wireOp",EDGE,"E31.filletArc"),sQuery(id+"F2.wireOp",EDGE,"E32"),sQuery(id+"F2.wireOp",EDGE,"E33.filletArc")])],"isStart":false}),"instanceName":"1"});
            var sketch = newSketch(context, id + "F19", { "sketchPlane" : qUnion([Q0])});
            skCircle(sketch, "E52.cCircle", {"center": v(45.68, 65.56) * mm, "radius": 2.75 * mm, "construction": true});
            skLineSegment(sketch, "E52.0", {"start": v(48.75, 64.74) * mm, "end": v(46.5, 62.5) * mm});
            skLineSegment(sketch, "E52.1", {"start": v(46.5, 62.5) * mm, "end": v(43.44, 63.31) * mm});
            skLineSegment(sketch, "E52.2", {"start": v(43.44, 63.31) * mm, "end": v(42.62, 66.38) * mm});
            skLineSegment(sketch, "E52.3", {"start": v(42.62, 66.38) * mm, "end": v(44.86, 68.63) * mm});
            skLineSegment(sketch, "E52.4", {"start": v(44.86, 68.63) * mm, "end": v(47.93, 67.8) * mm});
            skLineSegment(sketch, "E52.5", {"start": v(47.93, 67.8) * mm, "end": v(48.75, 64.74) * mm});
            skPoint(sketch, "E52.0.midPoint", {"position": v(47.63, 63.61) * mm});
            skCircle(sketch, "E53.cCircle", {"center": v(45.68, 35.86) * mm, "radius": 2.75 * mm, "construction": true});
            skLineSegment(sketch, "E53.0", {"start": v(47.27, 33.11) * mm, "end": v(44.1, 33.11) * mm});
            skLineSegment(sketch, "E53.1", {"start": v(44.1, 33.11) * mm, "end": v(42.5, 35.86) * mm});
            skLineSegment(sketch, "E53.2", {"start": v(42.5, 35.86) * mm, "end": v(44.1, 38.61) * mm});
            skLineSegment(sketch, "E53.3", {"start": v(44.1, 38.61) * mm, "end": v(47.27, 38.61) * mm});
            skLineSegment(sketch, "E53.4", {"start": v(47.27, 38.61) * mm, "end": v(48.86, 35.86) * mm});
            skLineSegment(sketch, "E53.5", {"start": v(48.86, 35.86) * mm, "end": v(47.27, 33.11) * mm});
            skPoint(sketch, "E53.0.midPoint", {"position": v(45.68, 33.11) * mm});
            skCircle(sketch, "E54.cCircle", {"center": v(15.98, 35.86) * mm, "radius": 2.75 * mm, "construction": true});
            skLineSegment(sketch, "E54.0", {"start": v(19.15, 35.67) * mm, "end": v(17.4, 33.02) * mm});
            skLineSegment(sketch, "E54.1", {"start": v(17.4, 33.02) * mm, "end": v(14.23, 33.21) * mm});
            skLineSegment(sketch, "E54.2", {"start": v(14.23, 33.21) * mm, "end": v(12.81, 36.05) * mm});
            skLineSegment(sketch, "E54.3", {"start": v(12.81, 36.05) * mm, "end": v(14.56, 38.7) * mm});
            skLineSegment(sketch, "E54.4", {"start": v(14.56, 38.7) * mm, "end": v(17.73, 38.51) * mm});
            skLineSegment(sketch, "E54.5", {"start": v(17.73, 38.51) * mm, "end": v(19.15, 35.67) * mm});
            skPoint(sketch, "E54.0.midPoint", {"position": v(18.28, 34.35) * mm});
            skCircle(sketch, "E55.cCircle", {"center": v(15.98, 65.56) * mm, "radius": 2.75 * mm, "construction": true});
            skLineSegment(sketch, "E55.0", {"start": v(19.15, 65.37) * mm, "end": v(17.4, 62.72) * mm});
            skLineSegment(sketch, "E55.1", {"start": v(17.4, 62.72) * mm, "end": v(14.23, 62.9) * mm});
            skLineSegment(sketch, "E55.2", {"start": v(14.23, 62.9) * mm, "end": v(12.81, 65.75) * mm});
            skLineSegment(sketch, "E55.3", {"start": v(12.81, 65.75) * mm, "end": v(14.56, 68.4) * mm});
            skLineSegment(sketch, "E55.4", {"start": v(14.56, 68.4) * mm, "end": v(17.73, 68.2) * mm});
            skLineSegment(sketch, "E55.5", {"start": v(17.73, 68.2) * mm, "end": v(19.15, 65.37) * mm});
            skPoint(sketch, "E55.0.midPoint", {"position": v(18.28, 64.04) * mm});
            skSolve(sketch);
        }
        {
            var Q0;
            Q0=makeQuery(id+"F19.imprint","IMPRINT",FACE,{"disambiguationData":[TD([[makeQuery(id+"F19.imprint","IMPRINT",EDGE,{"derivedFrom":sQuery(id+"F19.wireOp",EDGE,"E55.0")}),-1.0]])]});
            var Q1;
            Q1=makeQuery(id+"F19.imprint","IMPRINT",FACE,{"disambiguationData":[TD([[makeQuery(id+"F19.imprint","IMPRINT",EDGE,{"derivedFrom":sQuery(id+"F19.wireOp",EDGE,"E52.0")}),-1.0]])]});
            var Q2;
            Q2=makeQuery(id+"F19.imprint","IMPRINT",FACE,{"disambiguationData":[TD([[makeQuery(id+"F19.imprint","IMPRINT",EDGE,{"derivedFrom":sQuery(id+"F19.wireOp",EDGE,"E53.0")}),-1.0]])]});
            var Q3;
            Q3=makeQuery(id+"F19.imprint","IMPRINT",FACE,{"disambiguationData":[TD([[makeQuery(id+"F19.imprint","IMPRINT",EDGE,{"derivedFrom":sQuery(id+"F19.wireOp",EDGE,"E54.0")}),-1.0]])]});
            extrude(context, id + "F20", {"entities" : qUnion([Q0, Q1, Q2, Q3]), "oppositeDirection" : true, "depth" : 25 * mm, "offsetDistance" : 25 * mm});
        }
        {
            var Q0;
            Q0=makeQuery(id+"F20.opExtrude","SWEPT_BODY",BODY,{"disambiguationData":[OSD([sQuery(id+"F9.wireOp",EDGE,"E40"),sQuery(id+"F19.wireOp",EDGE,"E55.0"),sQuery(id+"F19.wireOp",EDGE,"E55.1"),sQuery(id+"F19.wireOp",EDGE,"E55.2"),sQuery(id+"F19.wireOp",EDGE,"E55.3"),sQuery(id+"F19.wireOp",EDGE,"E55.4"),sQuery(id+"F19.wireOp",EDGE,"E55.5")])]});
            var Q1;
            Q1=makeQuery(id+"F20.opExtrude","SWEPT_BODY",BODY,{"disambiguationData":[OSD([sQuery(id+"F9.wireOp",EDGE,"E39"),sQuery(id+"F19.wireOp",EDGE,"E54.0"),sQuery(id+"F19.wireOp",EDGE,"E54.1"),sQuery(id+"F19.wireOp",EDGE,"E54.2"),sQuery(id+"F19.wireOp",EDGE,"E54.3"),sQuery(id+"F19.wireOp",EDGE,"E54.4"),sQuery(id+"F19.wireOp",EDGE,"E54.5")])]});
            var Q2;
            Q2=makeQuery(id+"F20.opExtrude","SWEPT_BODY",BODY,{"disambiguationData":[OSD([sQuery(id+"F9.wireOp",EDGE,"E37"),sQuery(id+"F19.wireOp",EDGE,"E53.0"),sQuery(id+"F19.wireOp",EDGE,"E53.1"),sQuery(id+"F19.wireOp",EDGE,"E53.2"),sQuery(id+"F19.wireOp",EDGE,"E53.3"),sQuery(id+"F19.wireOp",EDGE,"E53.4"),sQuery(id+"F19.wireOp",EDGE,"E53.5")])]});
            var Q3;
            Q3=makeQuery(id+"F20.opExtrude","SWEPT_BODY",BODY,{"disambiguationData":[OSD([sQuery(id+"F9.wireOp",EDGE,"E38"),sQuery(id+"F19.wireOp",EDGE,"E52.0"),sQuery(id+"F19.wireOp",EDGE,"E52.1"),sQuery(id+"F19.wireOp",EDGE,"E52.2"),sQuery(id+"F19.wireOp",EDGE,"E52.3"),sQuery(id+"F19.wireOp",EDGE,"E52.4"),sQuery(id+"F19.wireOp",EDGE,"E52.5")])]});
            transform(context, id + "F21", {"entities" : qUnion([Q0, Q1, Q2, Q3]), "transformType" : TransformType.TRANSLATION_3D, "dx" : 0 * mm, "dy" : 4 * mm, "dz" : 0 * mm, "makeCopy" : false});
        }
        {
            var Q0;
            Q0=makeQuery(id+"F20.opExtrude","SWEPT_BODY",BODY,{"disambiguationData":[OSD([sQuery(id+"F9.wireOp",EDGE,"E40"),sQuery(id+"F19.wireOp",EDGE,"E55.0"),sQuery(id+"F19.wireOp",EDGE,"E55.1"),sQuery(id+"F19.wireOp",EDGE,"E55.2"),sQuery(id+"F19.wireOp",EDGE,"E55.3"),sQuery(id+"F19.wireOp",EDGE,"E55.4"),sQuery(id+"F19.wireOp",EDGE,"E55.5")])]});
            var Q1;
            Q1=makeQuery(id+"F20.opExtrude","SWEPT_BODY",BODY,{"disambiguationData":[OSD([sQuery(id+"F9.wireOp",EDGE,"E39"),sQuery(id+"F19.wireOp",EDGE,"E54.0"),sQuery(id+"F19.wireOp",EDGE,"E54.1"),sQuery(id+"F19.wireOp",EDGE,"E54.2"),sQuery(id+"F19.wireOp",EDGE,"E54.3"),sQuery(id+"F19.wireOp",EDGE,"E54.4"),sQuery(id+"F19.wireOp",EDGE,"E54.5")])]});
            var Q2;
            Q2=makeQuery(id+"F20.opExtrude","SWEPT_BODY",BODY,{"disambiguationData":[OSD([sQuery(id+"F9.wireOp",EDGE,"E37"),sQuery(id+"F19.wireOp",EDGE,"E53.0"),sQuery(id+"F19.wireOp",EDGE,"E53.1"),sQuery(id+"F19.wireOp",EDGE,"E53.2"),sQuery(id+"F19.wireOp",EDGE,"E53.3"),sQuery(id+"F19.wireOp",EDGE,"E53.4"),sQuery(id+"F19.wireOp",EDGE,"E53.5")])]});
            var Q3;
            Q3=makeQuery(id+"F20.opExtrude","SWEPT_BODY",BODY,{"disambiguationData":[OSD([sQuery(id+"F9.wireOp",EDGE,"E38"),sQuery(id+"F19.wireOp",EDGE,"E52.0"),sQuery(id+"F19.wireOp",EDGE,"E52.1"),sQuery(id+"F19.wireOp",EDGE,"E52.2"),sQuery(id+"F19.wireOp",EDGE,"E52.3"),sQuery(id+"F19.wireOp",EDGE,"E52.4"),sQuery(id+"F19.wireOp",EDGE,"E52.5")])]});
            var Q4;
            Q4=makeQuery(id+"F8.opLoft","SWEPT_BODY",BODY,{"disambiguationData":[OSD([sQuery(id+"F2.wireOp",EDGE,"E13"),sQuery(id+"F2.wireOp",EDGE,"E14.MirrorCS"),sQuery(id+"F2.wireOp",EDGE,"E15"),sQuery(id+"F2.wireOp",EDGE,"E16.MirrorCS"),sQuery(id+"F2.wireOp",EDGE,"E17"),sQuery(id+"F2.wireOp",EDGE,"E18.MirrorCS"),sQuery(id+"F2.wireOp",EDGE,"E19"),sQuery(id+"F2.wireOp",EDGE,"E20.MirrorCS"),sQuery(id+"F2.wireOp",EDGE,"E26.filletArc"),sQuery(id+"F2.wireOp",EDGE,"E27"),sQuery(id+"F2.wireOp",EDGE,"E28"),sQuery(id+"F2.wireOp",EDGE,"E29.filletArc"),sQuery(id+"F2.wireOp",EDGE,"E30"),sQuery(id+"F2.wireOp",EDGE,"E31.filletArc"),sQuery(id+"F2.wireOp",EDGE,"E32"),sQuery(id+"F2.wireOp",EDGE,"E33.filletArc")])]});
            booleanBodies(context, id + "F22", {"operationType" : BooleanOperationType.SUBTRACTION, "tools" : qUnion([Q0, Q1, Q2, Q3]), "targets" : qUnion([Q4])});
        }
        {
            var Q0;
            Q0=makeQuery(id+"F16.imprint","IMPRINT",FACE,{"disambiguationData":[TD([[makeQuery(id+"F16.imprint","IMPRINT",EDGE,{"derivedFrom":sQuery(id+"F16.wireOp",EDGE,"E51")}),1.0]])]});
            extrude(context, id + "F23", {"entities" : qUnion([Q0]), "oppositeDirection" : true, "depth" : 40 * mm, "offsetDistance" : 25 * mm});
        }
        {
            var Q0;
            Q0=makeQuery(id+"F23.opExtrude","SWEPT_BODY",BODY,{"disambiguationData":[OSD([sQuery(id+"F16.wireOp",EDGE,"E51")])]});
            var Q1;
            Q1=makeQuery(id+"F3.opExtrude","SWEPT_BODY",BODY,{"disambiguationData":[OSD([sQuery(id+"F2.wireOp",EDGE,"E13"),sQuery(id+"F2.wireOp",EDGE,"E14.MirrorCS"),sQuery(id+"F2.wireOp",EDGE,"E15"),sQuery(id+"F2.wireOp",EDGE,"E16.MirrorCS"),sQuery(id+"F2.wireOp",EDGE,"E17"),sQuery(id+"F2.wireOp",EDGE,"E18.MirrorCS"),sQuery(id+"F2.wireOp",EDGE,"E19"),sQuery(id+"F2.wireOp",EDGE,"E20.MirrorCS"),sQuery(id+"F2.wireOp",EDGE,"E26.filletArc"),sQuery(id+"F2.wireOp",EDGE,"E27"),sQuery(id+"F2.wireOp",EDGE,"E28"),sQuery(id+"F2.wireOp",EDGE,"E29.filletArc"),sQuery(id+"F2.wireOp",EDGE,"E30"),sQuery(id+"F2.wireOp",EDGE,"E31.filletArc"),sQuery(id+"F2.wireOp",EDGE,"E32"),sQuery(id+"F2.wireOp",EDGE,"E33.filletArc")])]});
            var Q2;
            Q2=makeQuery(id+"F8.opLoft","SWEPT_BODY",BODY,{"disambiguationData":[OSD([sQuery(id+"F2.wireOp",EDGE,"E13"),sQuery(id+"F2.wireOp",EDGE,"E14.MirrorCS"),sQuery(id+"F2.wireOp",EDGE,"E15"),sQuery(id+"F2.wireOp",EDGE,"E16.MirrorCS"),sQuery(id+"F2.wireOp",EDGE,"E17"),sQuery(id+"F2.wireOp",EDGE,"E18.MirrorCS"),sQuery(id+"F2.wireOp",EDGE,"E19"),sQuery(id+"F2.wireOp",EDGE,"E20.MirrorCS"),sQuery(id+"F2.wireOp",EDGE,"E26.filletArc"),sQuery(id+"F2.wireOp",EDGE,"E27"),sQuery(id+"F2.wireOp",EDGE,"E28"),sQuery(id+"F2.wireOp",EDGE,"E29.filletArc"),sQuery(id+"F2.wireOp",EDGE,"E30"),sQuery(id+"F2.wireOp",EDGE,"E31.filletArc"),sQuery(id+"F2.wireOp",EDGE,"E32"),sQuery(id+"F2.wireOp",EDGE,"E33.filletArc")])]});
            var Q3;
            Q3=makeQuery(id+"F4.opPattern","COPY",BODY,{"derivedFrom":makeQuery(id+"F3.opExtrude","SWEPT_BODY",BODY,{"disambiguationData":[OSD([sQuery(id+"F2.wireOp",EDGE,"E13"),sQuery(id+"F2.wireOp",EDGE,"E14.MirrorCS"),sQuery(id+"F2.wireOp",EDGE,"E15"),sQuery(id+"F2.wireOp",EDGE,"E16.MirrorCS"),sQuery(id+"F2.wireOp",EDGE,"E17"),sQuery(id+"F2.wireOp",EDGE,"E18.MirrorCS"),sQuery(id+"F2.wireOp",EDGE,"E19"),sQuery(id+"F2.wireOp",EDGE,"E20.MirrorCS"),sQuery(id+"F2.wireOp",EDGE,"E26.filletArc"),sQuery(id+"F2.wireOp",EDGE,"E27"),sQuery(id+"F2.wireOp",EDGE,"E28"),sQuery(id+"F2.wireOp",EDGE,"E29.filletArc"),sQuery(id+"F2.wireOp",EDGE,"E30"),sQuery(id+"F2.wireOp",EDGE,"E31.filletArc"),sQuery(id+"F2.wireOp",EDGE,"E32"),sQuery(id+"F2.wireOp",EDGE,"E33.filletArc")])]}),"instanceName":"1"});
            booleanBodies(context, id + "F24", {"operationType" : BooleanOperationType.SUBTRACTION, "tools" : qUnion([Q0]), "targets" : qUnion([Q1, Q2, Q3])});
        }
    });
